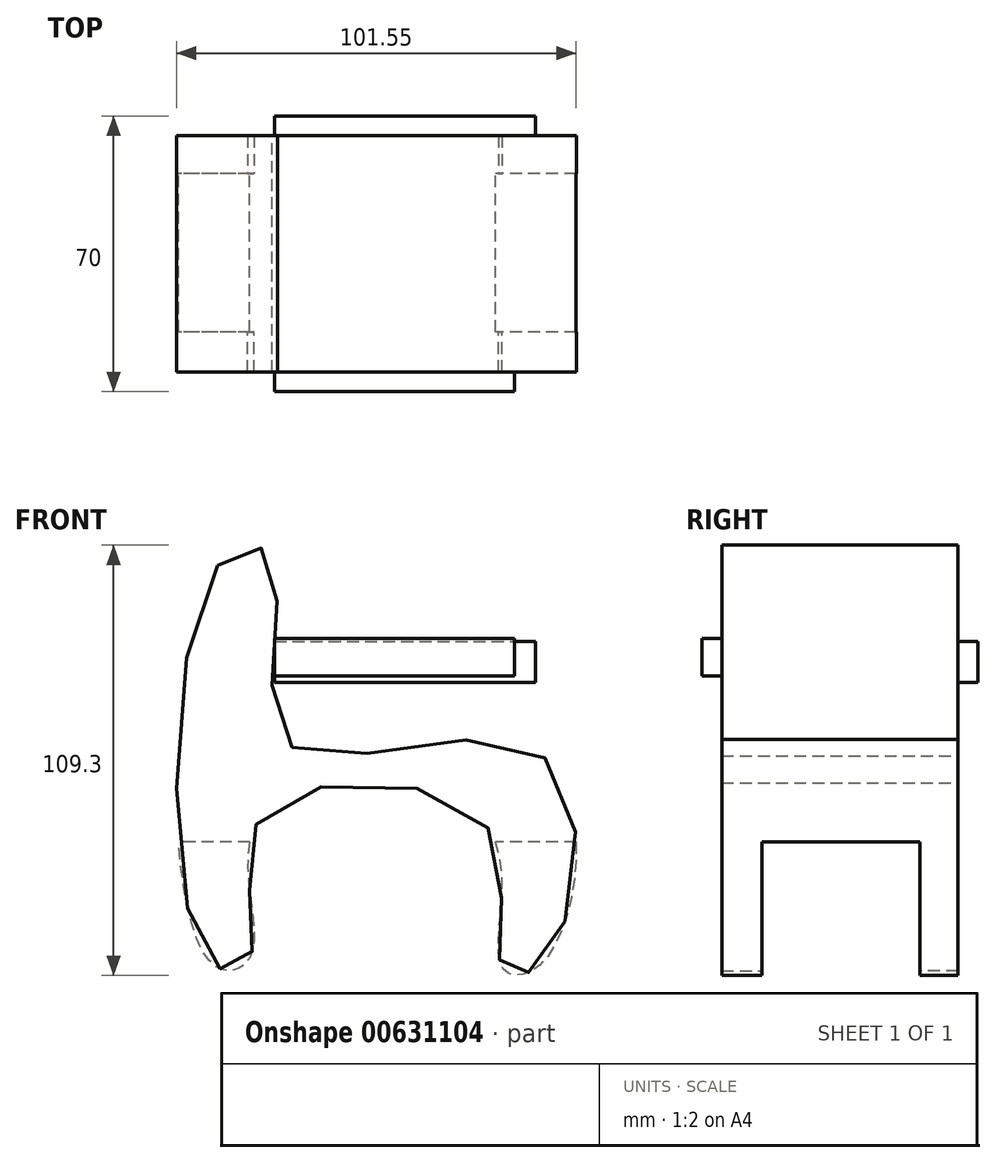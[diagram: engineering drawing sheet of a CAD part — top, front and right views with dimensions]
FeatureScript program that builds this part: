
annotation { "Feature Type Name" : "Feature", "Feature Type Description" : "" }
export const myFeature = defineFeature(function(context is Context, id is Id, definition is map)
    precondition{}
    {
        {
            var Q0;
            Q0=qCreatedBy(makeId("Front.planeOp"),FACE);
            var sketch = newSketch(context, id + "F0", { "sketchPlane" : qUnion([Q0])});
            skFitSpline(sketch, "E0", {"points": [v(-52.39, 55.08) * mm, v(-38.46, 56.03) * mm, v(-34.34, 9.5) * mm, v(28.96, 7.6) * mm, v(31.18, -44.63) * mm, v(19.78, -46.85) * mm, v(15.67, -10.76) * mm, v(-41.3, -8.86) * mm, v(-43.84, -43.68) * mm, v(-54.6, -45.27) * mm, v(-52.39, 55.08) * mm]});
            skSolve(sketch);
        }
        {
            var Q0;
            Q0=qCreatedBy(makeId("Right.planeOp"),FACE);
            var sketch = newSketch(context, id + "F1", { "sketchPlane" : qUnion([Q0])});
            skLineSegment(sketch, "E1.bottom", {"start": v(-49.86, -15.2) * mm, "end": v(-9.65, -15.2) * mm});
            skLineSegment(sketch, "E1.top", {"start": v(-49.86, -51.91) * mm, "end": v(-9.65, -51.91) * mm});
            skLineSegment(sketch, "E1.left", {"start": v(-49.86, -15.2) * mm, "end": v(-49.86, -51.91) * mm});
            skLineSegment(sketch, "E1.right", {"start": v(-9.65, -15.2) * mm, "end": v(-9.65, -51.91) * mm});
            skSolve(sketch);
        }
        {
            var Q0;
            Q0 = qSketchRegion(id + "F0", true);
            extrude(context, id + "F2", {"entities" : qUnion([Q0]), "depth" : 60 * mm, "offsetDistance" : 25 * mm});
        }
        {
            var Q0;
            Q0 = qSketchRegion(id + "F1", true);
            extrude(context, id + "F3", {"entities" : qUnion([Q0]), "operationType" : NewBodyOperationType.REMOVE, "endBound" : BoundingType.THROUGH_ALL, "depth" : 50 * mm, "offsetDistance" : 25 * mm, "hasSecondDirection" : true, "secondDirectionOppositeDirection" : true, "secondDirectionDepth" : 80 * mm});
        }
        {
            var Q0;
            Q0=makeQuery(id+"F2.opExtrude","CAP_FACE",FACE,{"disambiguationData":[OSD([sQuery(id+"F0.wireOp",EDGE,"E0")])],"isStart":false});
            var sketch = newSketch(context, id + "F4", { "sketchPlane" : qUnion([Q0])});
            skLineSegment(sketch, "E2.bottom", {"start": v(-37.9, 36.55) * mm, "end": v(23.01, 36.55) * mm});
            skLineSegment(sketch, "E2.top", {"start": v(-37.9, 26.97) * mm, "end": v(23.01, 26.97) * mm});
            skLineSegment(sketch, "E2.left", {"start": v(-37.9, 36.55) * mm, "end": v(-37.9, 26.97) * mm});
            skLineSegment(sketch, "E2.right", {"start": v(23.01, 36.55) * mm, "end": v(23.01, 26.97) * mm});
            skSolve(sketch);
        }
        {
            var Q0;
            Q0 = qSketchRegion(id + "F4", true);
            extrude(context, id + "F5", {"entities" : qUnion([Q0]), "depth" : 5 * mm, "offsetDistance" : 25 * mm});
        }
        {
            var Q0;
            Q0=makeQuery(id+"F2.opExtrude","CAP_FACE",FACE,{"disambiguationData":[OSD([sQuery(id+"F0.wireOp",EDGE,"E0")])],"isStart":true});
            var sketch = newSketch(context, id + "F6", { "sketchPlane" : qUnion([Q0])});
            skLineSegment(sketch, "E3.bottom", {"start": v(37.96, 35.73) * mm, "end": v(-28.33, 35.73) * mm});
            skLineSegment(sketch, "E3.top", {"start": v(37.96, 25.35) * mm, "end": v(-28.33, 25.35) * mm});
            skLineSegment(sketch, "E3.left", {"start": v(37.96, 35.73) * mm, "end": v(37.96, 25.35) * mm});
            skLineSegment(sketch, "E3.right", {"start": v(-28.33, 35.73) * mm, "end": v(-28.33, 25.35) * mm});
            skSolve(sketch);
        }
        {
            var Q0;
            Q0 = qSketchRegion(id + "F6", true);
            extrude(context, id + "F7", {"entities" : qUnion([Q0]), "depth" : 5 * mm, "offsetDistance" : 25 * mm});
        }
    });
